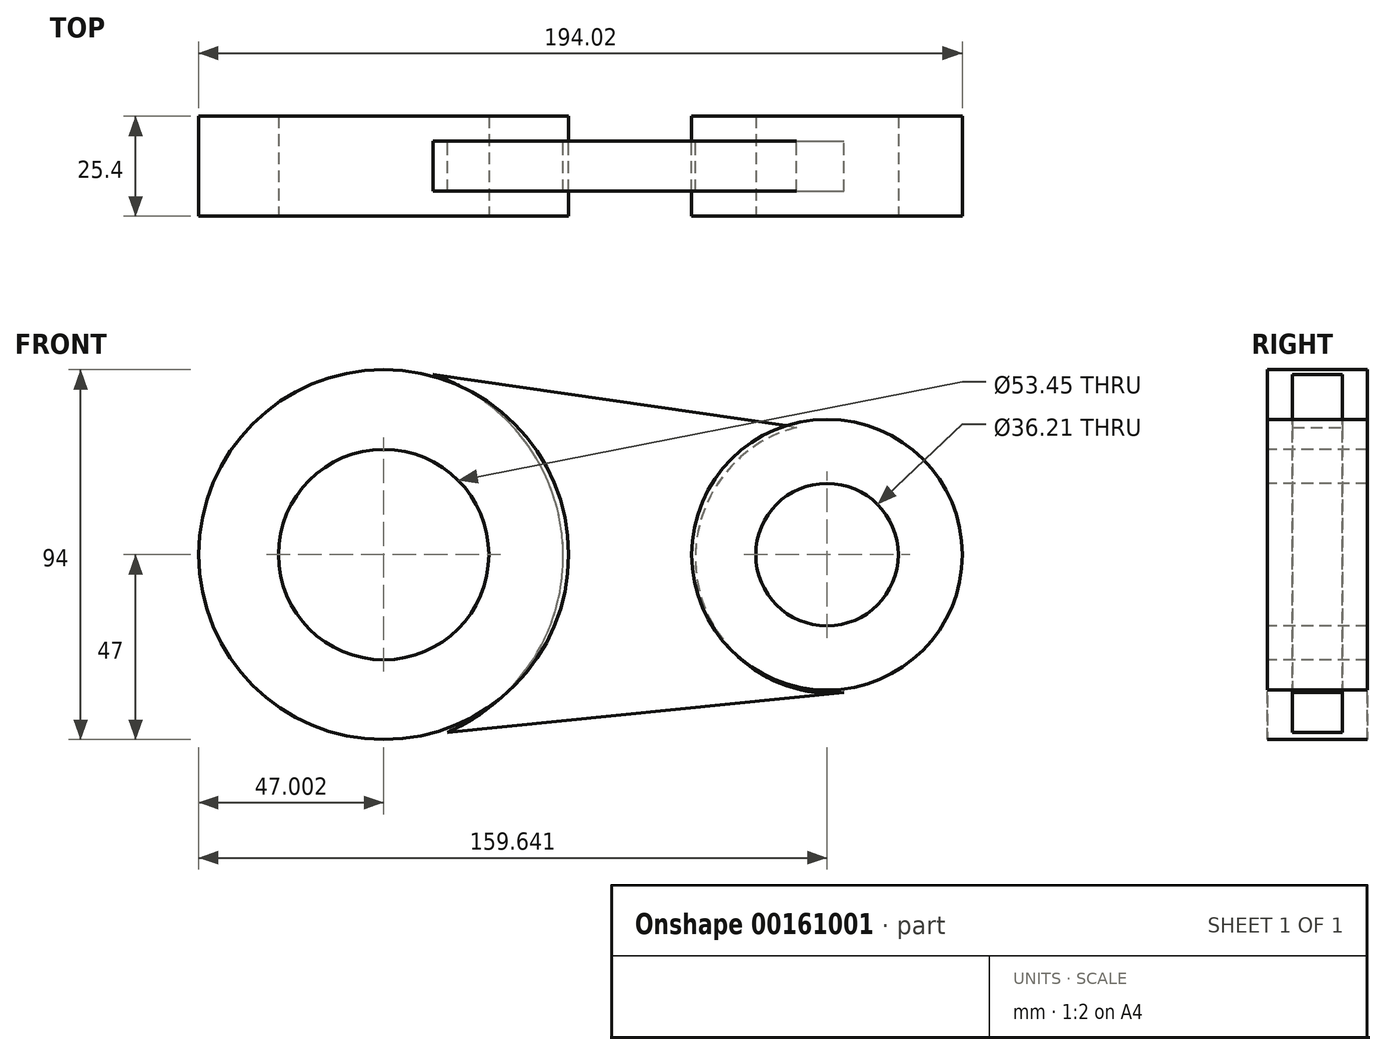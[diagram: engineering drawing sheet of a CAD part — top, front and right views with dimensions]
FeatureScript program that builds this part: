
annotation { "Feature Type Name" : "Feature", "Feature Type Description" : "" }
export const myFeature = defineFeature(function(context is Context, id is Id, definition is map)
    precondition{}
    {
        {
            var Q0;
            Q0=qCreatedBy(makeId("Front.planeOp"),FACE);
            var sketch = newSketch(context, id + "F0", { "sketchPlane" : qUnion([Q0])});
            skCircle(sketch, "E0", {"center": v(-68.39, 0) * mm, "radius": 47 * mm});
            skCircle(sketch, "E1", {"center": v(44.25, 0) * mm, "radius": 34.38 * mm});
            skLineSegment(sketch, "E2", {"start": v(-58.92, 46.03) * mm, "end": v(43.35, 34.37) * mm});
            skLineSegment(sketch, "E3", {"start": v(-56.87, -45.56) * mm, "end": v(47.96, -34.18) * mm});
            skSolve(sketch);
        }
        {
            var Q0;
            {var subQ0=sQuery(id+"F0.wireOp",EDGE,"E0");var subQ1=makeQuery(id+"F0.imprint","INTERSECT",VERTEX,{"derivedFrom":[subQ0,sQuery(id+"F0.wireOp",EDGE,"E2")]});Q0=makeQuery(id+"F0.imprint","IMPRINT",FACE,{"disambiguationData":[TD([[makeQuery(id+"F0.imprint","IMPRINT",EDGE,{"disambiguationData":[TD([[subQ1,-1.0]])],"derivedFrom":subQ0}),1.0]])]});}
            var Q1;
            {var subQ0=sQuery(id+"F0.wireOp",EDGE,"E1");var subQ1=makeQuery(id+"F0.imprint","INTERSECT",VERTEX,{"derivedFrom":[subQ0,sQuery(id+"F0.wireOp",EDGE,"E2")]});Q1=makeQuery(id+"F0.imprint","IMPRINT",FACE,{"disambiguationData":[TD([[makeQuery(id+"F0.imprint","IMPRINT",EDGE,{"disambiguationData":[TD([[subQ1,-1.0]])],"derivedFrom":subQ0}),1.0]])]});}
            extrude(context, id + "F1", {"entities" : qUnion([Q0, Q1]), "endBound" : BoundingType.SYMMETRIC, "depth" : 25.4 * mm});
        }
        {
            var Q0;
            Q0=qCreatedBy(makeId("Front.planeOp"),FACE);
            var sketch = newSketch(context, id + "F2", { "sketchPlane" : qUnion([Q0])});
            skLineSegment(sketch, "E4", {"start": v(-55.77, 45.74) * mm, "end": v(36.43, 32.36) * mm});
            skLineSegment(sketch, "E5", {"start": v(-52.16, -45.15) * mm, "end": v(48.56, -35.01) * mm});
            skArc(sketch, "E6", {"start": v(-52.16, -45.15) * mm, "mid": v(-22.8, 1.54) * mm, "end": v(-55.77, 45.74) * mm});
            skArc(sketch, "E7", {"start": v(36.43, 32.36) * mm, "mid": v(11.33, -6.94) * mm, "end": v(48.56, -35.01) * mm});
            skSolve(sketch);
        }
        {
            var Q0;
            Q0 = qSketchRegion(id + "F2", true);
            extrude(context, id + "F3", {"entities" : qUnion([Q0]), "endBound" : BoundingType.SYMMETRIC, "depth" : 12.7 * mm});
        }
        {
            var Q0;
            Q0=makeQuery(id+"F1.opExtrude","CAP_FACE",FACE,{"disambiguationData":[OSD([sQuery(id+"F0.wireOp",EDGE,"E0")])],"isStart":false});
            var sketch = newSketch(context, id + "F4", { "sketchPlane" : qUnion([Q0])});
            skCircle(sketch, "E8", {"center": v(-68.39, 0) * mm, "radius": 26.72 * mm});
            skSolve(sketch);
        }
        {
            var Q0;
            Q0=makeQuery(id+"F4.imprint","IMPRINT",FACE,{"disambiguationData":[TD([[makeQuery(id+"F4.imprint","IMPRINT",EDGE,{"derivedFrom":sQuery(id+"F4.wireOp",EDGE,"E8")}),1.0]])]});
            extrude(context, id + "F5", {"entities" : qUnion([Q0]), "operationType" : NewBodyOperationType.REMOVE, "endBound" : BoundingType.THROUGH_ALL, "oppositeDirection" : true, "depth" : 25.4 * mm});
        }
        {
            var Q0;
            Q0=makeQuery(id+"F1.opExtrude","CAP_FACE",FACE,{"disambiguationData":[OSD([sQuery(id+"F0.wireOp",EDGE,"E1")])],"isStart":false});
            var sketch = newSketch(context, id + "F6", { "sketchPlane" : qUnion([Q0])});
            skCircle(sketch, "E9", {"center": v(44.25, 0) * mm, "radius": 18.1 * mm});
            skSolve(sketch);
        }
        {
            var Q0;
            Q0 = qSketchRegion(id + "F6", true);
            extrude(context, id + "F7", {"entities" : qUnion([Q0]), "operationType" : NewBodyOperationType.REMOVE, "endBound" : BoundingType.THROUGH_ALL, "oppositeDirection" : true, "depth" : 25.4 * mm});
        }
    });
